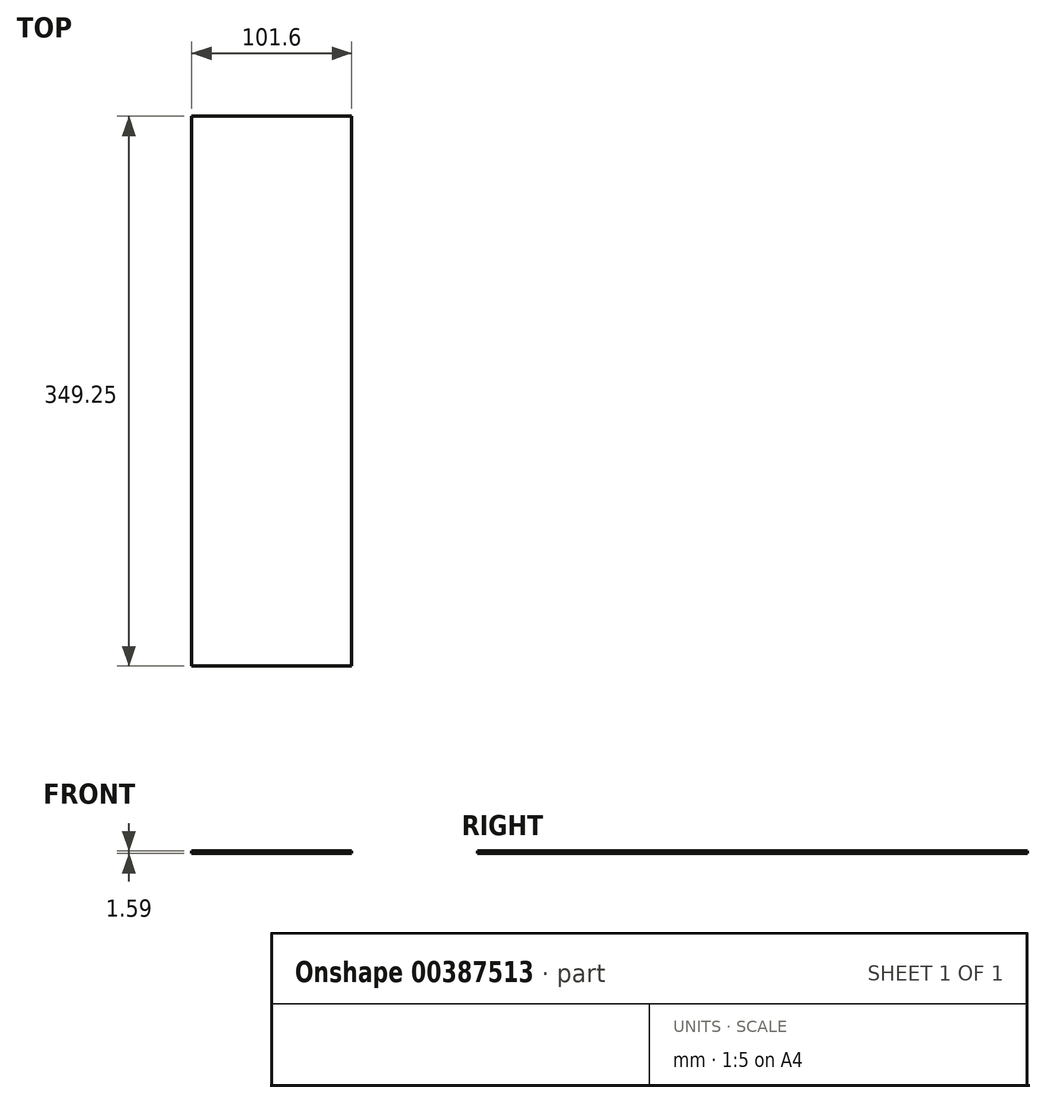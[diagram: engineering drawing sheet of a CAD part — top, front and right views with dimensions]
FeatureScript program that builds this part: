
annotation { "Feature Type Name" : "Feature", "Feature Type Description" : "" }
export const myFeature = defineFeature(function(context is Context, id is Id, definition is map)
    precondition{}
    {
        {
            var Q0;
            Q0=qCreatedBy(makeId("Top.planeOp"),FACE);
            var sketch = newSketch(context, id + "F0", { "sketchPlane" : qUnion([Q0])});
            skLineSegment(sketch, "E0.bottom", {"start": v(0, 0) * mm, "end": v(101.6, 0) * mm});
            skLineSegment(sketch, "E0.top", {"start": v(0, 349.25) * mm, "end": v(101.6, 349.25) * mm});
            skLineSegment(sketch, "E0.left", {"start": v(0, 0) * mm, "end": v(0, 349.25) * mm});
            skLineSegment(sketch, "E0.right", {"start": v(101.6, 0) * mm, "end": v(101.6, 349.25) * mm});
            skSolve(sketch);
        }
        {
            var Q0;
            Q0 = qSketchRegion(id + "F0", true);
            extrude(context, id + "F1", {"entities" : qUnion([Q0]), "depth" : 1.59 * mm});
        }
    });
